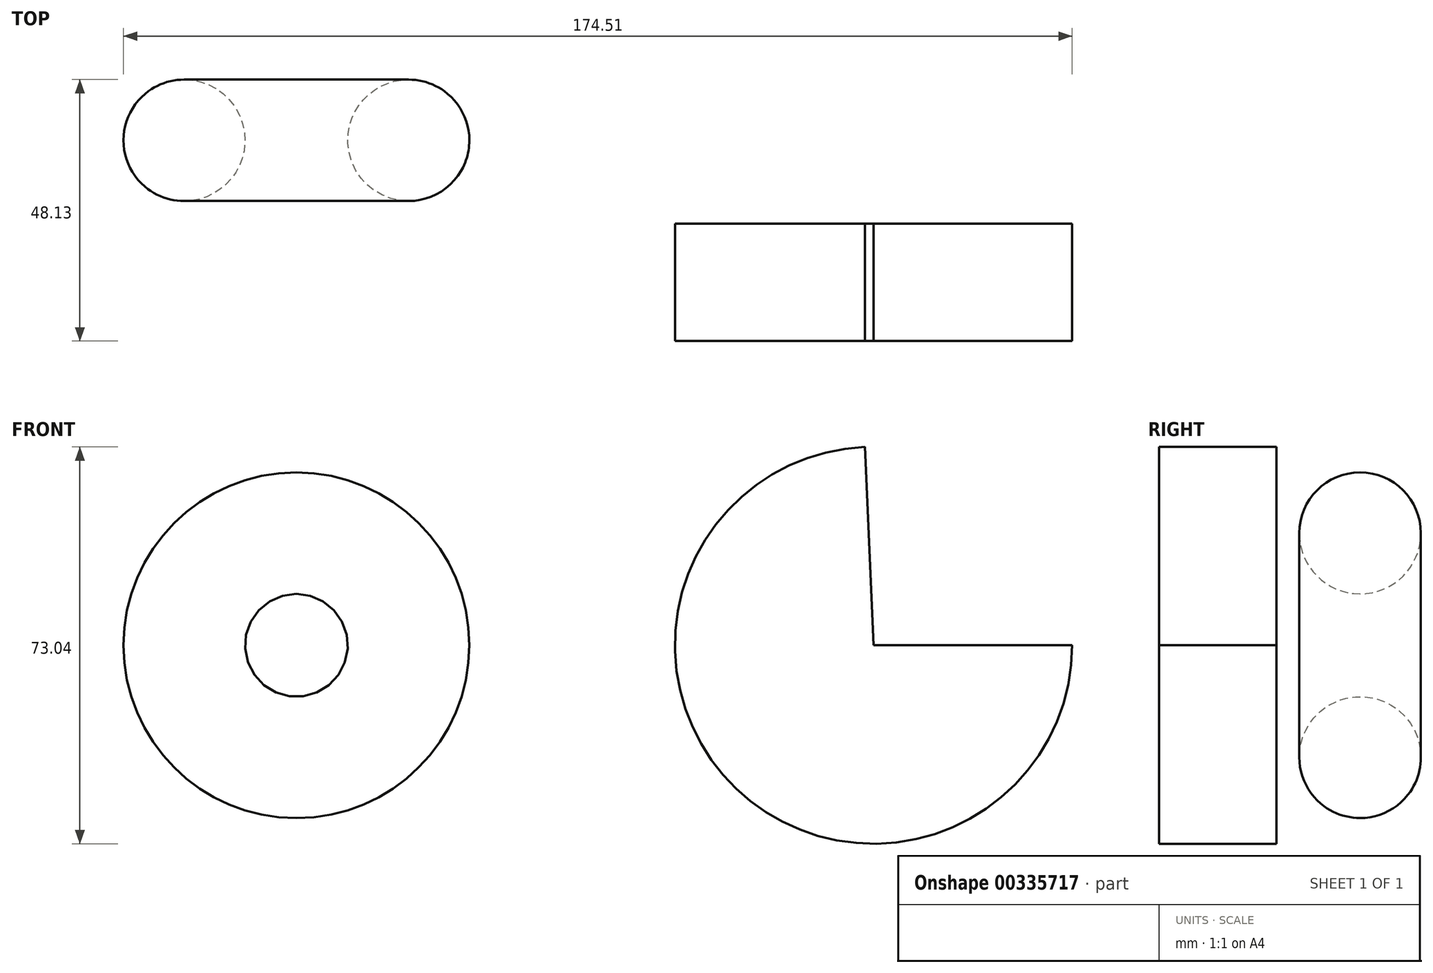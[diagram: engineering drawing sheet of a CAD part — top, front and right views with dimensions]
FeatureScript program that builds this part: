
annotation { "Feature Type Name" : "Feature", "Feature Type Description" : "" }
export const myFeature = defineFeature(function(context is Context, id is Id, definition is map)
    precondition{}
    {
        {
            var Q0;
            Q0=qCreatedBy(makeId("Top.planeOp"),FACE);
            var sketch = newSketch(context, id + "F0", { "sketchPlane" : qUnion([Q0])});
            skCircle(sketch, "E0", {"center": v(-62.28, 52.52) * mm, "radius": 11.18 * mm});
            skLineSegment(sketch, "E1.bottom", {"start": v(23.25, 37.16) * mm, "end": v(59.79, 37.16) * mm});
            skLineSegment(sketch, "E1.top", {"start": v(23.25, 15.57) * mm, "end": v(59.79, 15.57) * mm});
            skLineSegment(sketch, "E1.left", {"start": v(23.25, 37.16) * mm, "end": v(23.25, 15.57) * mm});
            skLineSegment(sketch, "E1.right", {"start": v(59.79, 37.16) * mm, "end": v(59.79, 15.57) * mm});
            skLineSegment(sketch, "E2", {"start": v(-55, -17.45) * mm, "end": v(-20.95, -29.08) * mm});
            skLineSegment(sketch, "E3", {"start": v(-20.95, -29.08) * mm, "end": v(-20.95, -63.13) * mm});
            skLineSegment(sketch, "E4", {"start": v(-20.95, -63.13) * mm, "end": v(-59.98, -69.35) * mm});
            skLineSegment(sketch, "E5", {"start": v(-59.98, -69.35) * mm, "end": v(-55, -17.45) * mm});
            skLineSegment(sketch, "E6", {"start": v(-44.62, -31.99) * mm, "end": v(-50.43, -55.24) * mm});
            skLineSegment(sketch, "E7", {"start": v(-50.43, -55.24) * mm, "end": v(-37.93, -58.36) * mm});
            skLineSegment(sketch, "E8", {"start": v(-37.93, -58.36) * mm, "end": v(-44.62, -31.99) * mm});
            skLineSegment(sketch, "E9", {"start": v(-82.91, 71.7) * mm, "end": v(-82.91, 30.26) * mm, "construction": true});
            skSolve(sketch);
        }
        {
            var Q0;
            Q0=makeQuery(id+"F0.imprint","IMPRINT",FACE,{"disambiguationData":[TD([[makeQuery(id+"F0.imprint","IMPRINT",EDGE,{"derivedFrom":sQuery(id+"F0.wireOp",EDGE,"E1.bottom")}),-1.0]])]});
            var Q1;
            Q1=sQuery(id+"F0.wireOp",EDGE,"E1.left");
            revolve(context, id + "F1", {"entities" : qUnion([Q0]), "axis" : qUnion([Q1]), "revolveType" : RevolveType.ONE_DIRECTION, "oppositeDirection" : true, "angle" : 267.54 * degree});
        }
        {
            var Q0;
            Q0=makeQuery(id+"F0.imprint","IMPRINT",FACE,{"disambiguationData":[TD([[makeQuery(id+"F0.imprint","IMPRINT",EDGE,{"derivedFrom":sQuery(id+"F0.wireOp",EDGE,"E0")}),1.0]])]});
            var Q1;
            Q1=sQuery(id+"F0.wireOp",EDGE,"E9");
            revolve(context, id + "F2", {"entities" : qUnion([Q0]), "axis" : qUnion([Q1]), "revolveType" : RevolveType.FULL});
        }
    });
